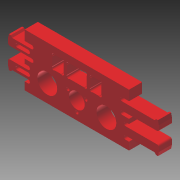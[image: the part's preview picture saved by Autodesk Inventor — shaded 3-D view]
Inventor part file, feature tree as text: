
AUTODESK INVENTOR PART (.ipt)
format: ipt  version: 2012 SP1 (Build 160190100, 190)  size: 241,152 bytes
history: native  units: in
note: dims shown in document units (in); Inventor stores cm internally (conversion verified against a paired STEP export)
features: other x4, extrude x2
ambient origin geometry x8: Origin, YZ Plane, XZ Plane, XY Plane, X Axis, Y Axis, Z Axis, Center Point
bodies: Solid1 (feature_tree)
feature tree (6):
  other  "skeleton.ipt"
  other  "DRILL-THROUGH"
  other  "STOCK_12MM"
  extrude  "Extrusion1"  Depth=0.3937in
  extrude  "Extrusion2"  Depth=0.4724in
  other  "THROUGH-CUT"
